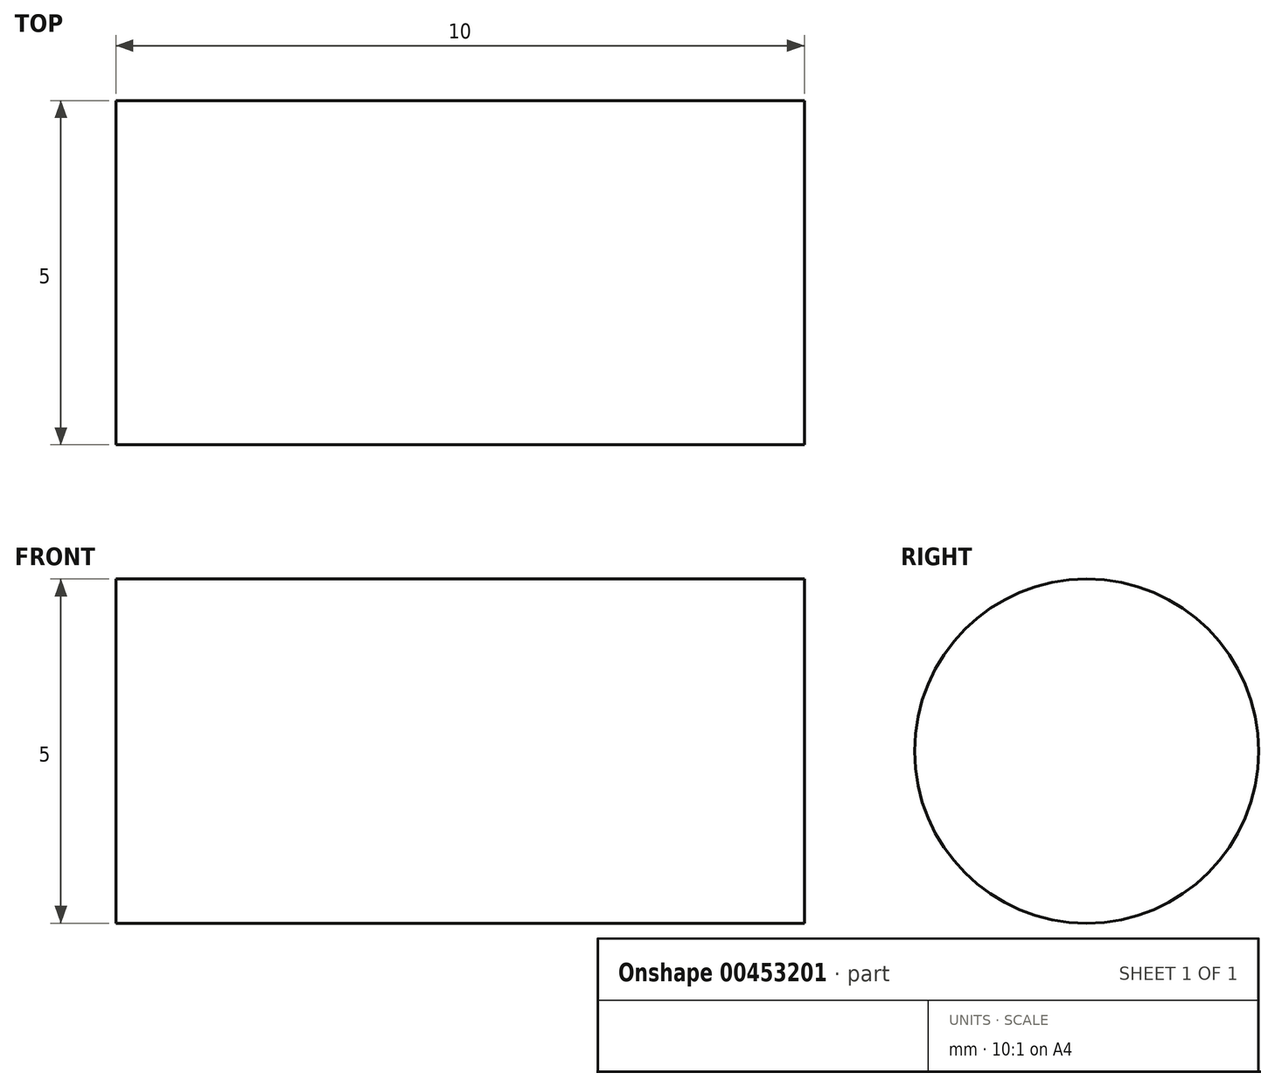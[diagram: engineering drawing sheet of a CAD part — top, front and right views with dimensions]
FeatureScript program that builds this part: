
annotation { "Feature Type Name" : "Feature", "Feature Type Description" : "" }
export const myFeature = defineFeature(function(context is Context, id is Id, definition is map)
    precondition{}
    {
        {
            var Q0;
            Q0=qCreatedBy(makeId("Right.planeOp"),FACE);
            var sketch = newSketch(context, id + "F0", { "sketchPlane" : qUnion([Q0])});
            skCircle(sketch, "E0", {"center": v(0, 0) * mm, "radius": 2.5 * mm});
            skSolve(sketch);
        }
        {
            var Q0;
            Q0=makeQuery(id+"F0.imprint","IMPRINT",FACE,{"disambiguationData":[TD([[makeQuery(id+"F0.imprint","IMPRINT",EDGE,{"derivedFrom":sQuery(id+"F0.wireOp",EDGE,"E0")}),1.0]])]});
            extrude(context, id + "F1", {"entities" : qUnion([Q0]), "depth" : 10 * mm});
        }
    });
